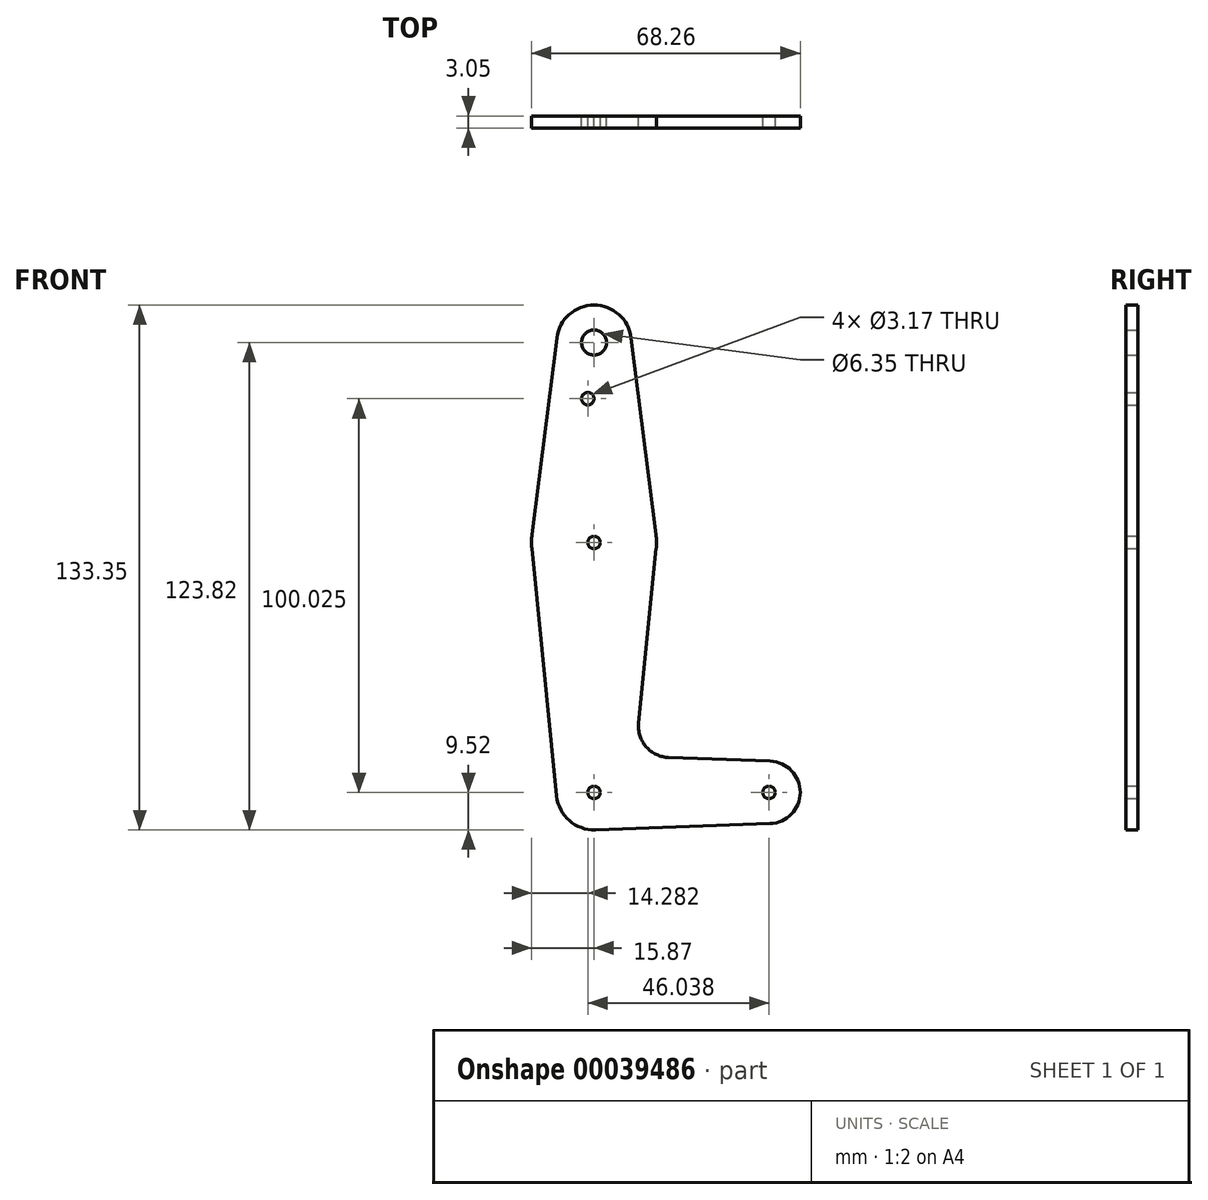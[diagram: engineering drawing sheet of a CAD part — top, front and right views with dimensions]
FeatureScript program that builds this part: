
annotation { "Feature Type Name" : "Feature", "Feature Type Description" : "" }
export const myFeature = defineFeature(function(context is Context, id is Id, definition is map)
    precondition{}
    {
        {
            var Q0;
            Q0=qCreatedBy(makeId("Front.planeOp"),FACE);
            var sketch = newSketch(context, id + "F0", { "sketchPlane" : qUnion([Q0])});
            skLineSegment(sketch, "E0", {"start": v(0, 0) * mm, "end": v(0, 114.3) * mm, "construction": true});
            skLineSegment(sketch, "E1", {"start": v(0, 0) * mm, "end": v(44.45, 0) * mm});
            skCircle(sketch, "E2", {"center": v(0, 114.3) * mm, "radius": 9.52 * mm});
            skCircle(sketch, "E3", {"center": v(44.45, 0) * mm, "radius": 7.94 * mm});
            skCircle(sketch, "E4", {"center": v(0, 0) * mm, "radius": 9.53 * mm});
            skCircle(sketch, "E5", {"center": v(0, 63.5) * mm, "radius": 15.88 * mm});
            skLineSegment(sketch, "E6", {"start": v(-9.45, 115.5) * mm, "end": v(-15.75, 65.48) * mm});
            skLineSegment(sketch, "E7", {"start": v(-15.8, 61.91) * mm, "end": v(-9.48, -0.95) * mm});
            skLineSegment(sketch, "E8", {"start": v(15.8, 61.91) * mm, "end": v(11.34, 17.6) * mm});
            skLineSegment(sketch, "E9", {"start": v(9.45, 115.5) * mm, "end": v(15.8, 65.13) * mm});
            skLineSegment(sketch, "E10", {"start": v(18.97, 8.85) * mm, "end": v(44.73, 7.93) * mm});
            skLineSegment(sketch, "E11", {"start": v(0.34, -9.52) * mm, "end": v(44.73, -7.93) * mm});
            skCircle(sketch, "E12", {"center": v(0, 114.3) * mm, "radius": 3.18 * mm});
            skCircle(sketch, "E13", {"center": v(0, 63.5) * mm, "radius": 1.59 * mm});
            skCircle(sketch, "E14", {"center": v(0, 0) * mm, "radius": 1.59 * mm});
            skCircle(sketch, "E15", {"center": v(44.45, 0) * mm, "radius": 1.59 * mm});
            skCircle(sketch, "E16", {"center": v(-1.59, 100.03) * mm, "radius": 1.59 * mm});
            skArc(sketch, "E17.filletArc", {"start": v(11.34, 17.6) * mm, "mid": v(13.26, 11.57) * mm, "end": v(18.97, 8.85) * mm});
            skSolve(sketch);
        }
        {
            var Q0;
            Q0 = qSketchRegion(id + "F0", true);
            extrude(context, id + "F1", {"entities" : qUnion([Q0]), "depth" : 3.05 * mm});
        }
    });
